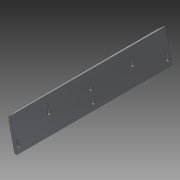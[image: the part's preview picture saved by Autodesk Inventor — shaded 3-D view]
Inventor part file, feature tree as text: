
AUTODESK INVENTOR PART (.ipt)
format: ipt  version: 2011 SP2 (Build 150309200, 309)  size: 1,090,560 bytes
history: native  units: mm
features: extrude x39, sketch x22, projected_geometry x14, fillet x12, mirror x2, pattern_linear x2, plane x1, chamfer x1, hole x1
ambient origin geometry x8: Origin, YZ Plane, XZ Plane, XY Plane, X Axis, Y Axis, Z Axis, Center Point
feature tree (94):
  sketch  "Sketch1"  dims[d0=200.0mm d1=200.0mm]
  extrude  "Extrusion3"  Depth=200.0mm
  extrude  "Extrusion4"  Depth=10.5mm
  extrude  "Extrusion5"  Depth=6.5mm
  extrude  "Extrusion6"  Depth=53.3mm
  extrude  "Extrusion7"  Depth=26.65mm
  sketch  "Sketch4"  dims[d6=6.5mm d8=53.3mm]
  extrude  "Extrusion8"  Depth=5.0mm
  extrude  "Extrusion9"  Depth=5.0mm
  extrude  "Extrusion10"  Depth=4.4mm
  plane  "Work Plane1"
  mirror  "Mirror1"
  sketch  "Sketch9"  dims[d9=53.3mm d10=26.65mm]
  sketch  "Sketch10"  dims[d11=26.65mm d13=5.0mm]
  extrude  "Extrusion16"  Depth=8.0mm
  extrude  "Extrusion17"  Depth=8.0mm
  extrude  "Extrusion18"  Depth=60.0mm
  extrude  "Extrusion19"  Depth=39.0mm
  extrude  "Extrusion20"  Depth=3.65mm
  extrude  "Extrusion21"  Depth=1.5mm
  extrude  "Extrusion22"  Depth=6.6mm
  sketch  "Sketch13"  dims[d18=4.4mm d19=8.0mm]
  extrude  "Extrusion26"  Depth=6.6mm
  extrude  "Extrusion27"  Depth=3.5mm
  extrude  "Extrusion30"  Depth=5.0mm
  extrude  "Extrusion32"  Depth=46.7mm
  extrude  "Extrusion33"  Depth=11.0mm TaperAngle=0.0deg
  extrude  "Extrusion34"  Depth=13.0mm
  chamfer  "Chamfer2"  Distance=36.8mm
  fillet  "Fillet1"  Radius=7.0mm
  extrude  "Extrusion35"  Depth=3.0mm
  extrude  "Extrusion36"  Depth=15.5mm
  sketch  "Sketch21"  dims[d28=1.6mm d29=3.65mm d30=3.65mm]
  extrude  "Extrusion37"  Depth=60.0mm TaperAngle=360.0deg
  extrude  "Extrusion39"  Depth=55.0mm TaperAngle=0.0deg
  extrude  "Extrusion40"  Depth=2.0mm
  fillet  "Fillet2"  Radius=2.0mm
  sketch  "Sketch28"  dims[d44=60.0mm d45=6.6mm]
  extrude  "Extrusion48"  Depth=3.65mm
  extrude  "Extrusion49"  Depth=3.65mm
  extrude  "Extrusion42"  Depth=55.0mm TaperAngle=0.0deg
  extrude  "Extrusion44"  Depth=36.8mm
  fillet  "Fillet4"  Radius=36.0mm
  mirror  "Mirror3"
  fillet  "Fillet3"  Radius=40.0mm
  extrude  "Extrusion45"  Depth=40.0mm TaperAngle=0.0deg
  sketch  "Sketch30"  dims[d49=12.061mm d50=5.0mm]
  extrude  "Extrusion46"  Depth=23.0mm TaperAngle=0.0deg
  extrude  "Extrusion47"  Depth=23.35mm
  hole  "Hole1"  [1 undecoded]
  fillet  "Fillet5"  Radius=2.8mm
  fillet  "Fillet6"  Radius=2.8mm
  fillet  "Fillet7"  Radius=2.8mm
  fillet  "Fillet8"  Radius=2.8mm
  fillet  "Fillet9"  Radius=32.757mm
  fillet  "Fillet10"  Radius=32.757mm
  fillet  "Fillet11"  Radius=80.957mm
  fillet  "Fillet12"  Radius=80.957mm
  extrude  "Extrusion50"  Depth=27.264mm
  extrude  "Extrusion51"  Depth=20.564mm
  sketch  "Sketch34"  dims[d65=38.0mm d66=36.8mm d67=7.0mm d68=3.0mm d69=15.5mm d70=60.0mm d72=360.0deg d74=55.0mm d75=0.0mm d76=2.0mm d77=2.0mm d78=3.65mm d79=3.65mm d80=55.0mm d81=0.0mm d82=36.8mm d83=36.0mm d84=40.0mm d85=0.0mm d86=40.0mm d87=0.0mm d88=23.0mm d89=0.0mm d90=23.35mm d91=6.15mm d119=2.8mm d120=2.8mm d121=2.8mm d122=2.8mm d135=32.757mm d136=32.757mm d137=80.957mm d138=80.957mm d139=27.264mm d140=20.564mm d141=34.936mm d142=35.936mm d143=2.0mm d144=11.0mm d145=11.0mm d146=2.0mm d147=11.0mm d148=11.0mm d149=2.0mm d150=2.0mm d155=6.0mm d156=6.0mm d157=6.0mm d158=6.0mm d159=3.0mm d160=3.0mm d161=3.0mm d162=3.0mm d163=6.0mm d164=6.0mm d165=3.0mm d166=3.0mm d167=6.0mm d168=6.0mm d169=3.0mm d170=3.0mm d181=3.0mm d182=2.5mm d184=0.0mm d185=0.0mm d186=200.0mm d187=0.0mm d188=200.0mm d189=0.0mm d190=58.0mm d191=0.0mm d192=18.0mm d193=0.0mm d194=40.0mm d195=0.0mm d196=1.570796mm d197=1.570796mm d198=220.0mm d199=220.0mm d200=10.0mm d201=10.0mm d202=5.0mm d203=7.0mm d204=0.0mm d205=0.0mm d215=32.1mm d231=5.0mm d233=12.0mm d234=0.0mm d239=20.0mm d240=0.0mm d256=6.0mm d257=167.0mm d258=6.2mm d259=6.0mm d260=0.0mm d262=22.75mm d266=10.0mm d267=38.9mm d268=5.5mm d269=32.1mm d272=10.0mm d273=12.2mm d276=12.0mm d277=0.0mm d278=28.5mm d279=10.3mm d280=0.0mm d281=5.0mm d282=0.0mm d283=0.5mm d284=5.3mm d285=45.0deg d286=1.0mm d287=5.0mm d288=0.0mm d289=3.0mm d290=3.0mm d291=10.0mm d292=0.0mm d293=6.15mm d294=4.4mm d295=2.0mm d296=3.0mm d297=10.0mm d298=0.0mm d306=41.0mm d307=0.0mm d308=6.0mm d309=6.0mm d310=2.575mm d311=2.575mm d312=2.0mm d313=2.0mm d315=8.956377mm d316=161.0mm d317=10.0mm d318=7.0mm d319=0.0mm d320=32.5mm d335=32.5mm d336=7.0mm d337=12.0mm d338=9.25mm d339=-0.872665mm d343=1.0mm d344=9.25mm d345=-0.872665mm d346=8.0mm d347=4.0mm d348=10.0mm d349=20.0mm d350=0.0mm d351=179.0mm d352=0.0mm d353=179.0mm d354=0.0mm d355=1.5mm d356=3.5mm d357=3.5mm d358=89.5mm d359=89.5mm d360=5.0mm d361=17.5mm d362=2.0mm d363=6.0mm d364=3.0mm d365=2.0mm d366=90.0deg d367=2.0mm d368=3.665191mm d369=6.0mm d370=6.0mm d371=6.0mm d372=6.0mm d373=6.0mm d376=6.0mm d377=2.0mm d378=2.0mm d379=2.0mm d380=3.0mm d382=3.0mm d383=3.0mm d384=3.0mm d386=55.0mm d387=0.0mm d388=40.0mm d389=0.0mm d390=26.0mm d391=69.0mm d392=48.0mm d393=3.0mm d394=13.0mm d395=13.0mm d396=3.0mm d397=1.0mm d398=0.5mm d399=0.5mm d400=1.0mm d401=0.5mm d402=1.0mm d403=15.0mm d404=1.0mm d405=10.0mm d406=0.0mm d407=10.0mm d408=0.0mm d409=3.0mm d410=3.0mm d411=2.0mm d412=2.0mm d416=3.0mm d431=4.0mm d432=0.0mm d433=0.5mm d434=-7.853982mm d439=30.0mm d441=86.0mm d445=3.0mm d446=3.0mm d447=2.0mm d448=2.0mm d449=2.5mm d450=2.5mm d451=0.5mm d452=0.0mm d453=0.5mm d454=-7.853982mm d455=30.0mm d457=48.029mm]
  extrude  "Extrusion53"  Depth=34.936mm
  extrude  "Extrusion54"  Depth=35.936mm
  pattern_linear  "Rectangular Pattern1"  Spacing1=2.0mm  [1 undecoded]
  extrude  "Extrusion57"  Depth=11.0mm
  extrude  "Extrusion58"  Depth=11.0mm
  pattern_linear  "Rectangular Pattern3"  Spacing1=2.0mm  [1 undecoded]
  sketch  "Sketch2"  dims[d2=10.5mm d3=10.5mm]
  sketch  "Sketch3"  dims[d4=57.861mm d5=6.5mm]
  projected_geometry  "Projected Loop1"
  projected_geometry  "Projected Loop7"
  sketch  "Sketch11"  dims[d14=5.0mm d15=5.0mm]
  sketch  "Sketch12"  dims[d16=6.15mm d17=4.4mm]
  projected_geometry  "Projected Loop8"
  sketch  "Sketch15"  dims[d20=5.0mm d21=8.0mm]
  projected_geometry  "Projected Loop9"
  sketch  "Sketch18"  dims[d22=5.0mm d23=60.0mm]
  projected_geometry  "Projected Loop11"
  sketch  "Sketch20"  dims[d25=138.0mm d27=39.0mm]
  projected_geometry  "Projected Loop12"
  sketch  "Sketch25"  dims[d31=3.0mm d32=0.5mm d34=1.5mm d36=5.0mm]
  sketch  "Sketch27"  dims[d37=3.0mm d38=5.0mm d39=8.15mm d41=6.6mm d42=1.5mm d43=0.5mm]
  projected_geometry  "Projected Loop16"
  sketch  "Sketch29"  dims[d47=11.6mm d48=3.5mm]
  sketch  "Sketch31"  dims[d56=8.15mm d57=46.7mm]
  projected_geometry  "Projected Loop17"
  projected_geometry  "Projected Loop18"
  projected_geometry  "Projected Loop19"
  projected_geometry  "Projected Loop20"
  projected_geometry  "Projected Loop21"
  projected_geometry  "Projected Loop22"
  projected_geometry  "Projected Loop23"
  sketch  "Sketch32"  dims[d58=4.0mm d59=0.0mm d60=11.0mm d61=0.0mm]
  sketch  "Sketch33"  dims[d62=55.0mm d63=0.0mm d64=13.0mm]
note: 3 required parameter values undecoded (feature->parameter linkage not recoverable at this tier; creation-order binding heuristic only, values carry confidence <= 0.55)
